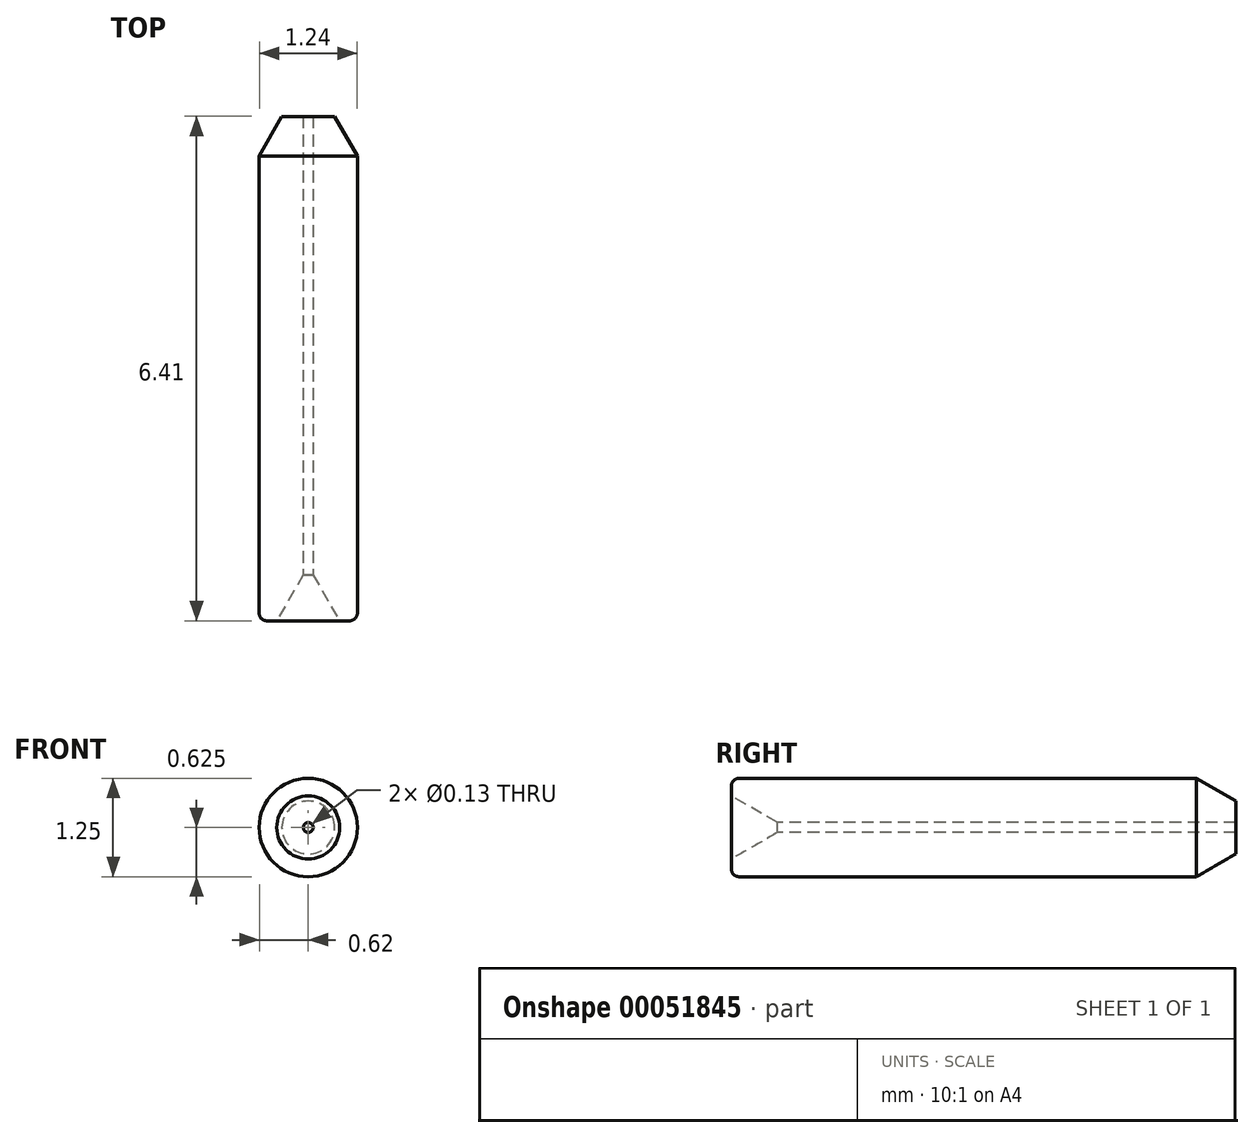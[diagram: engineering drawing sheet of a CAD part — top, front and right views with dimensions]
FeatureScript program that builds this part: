
annotation { "Feature Type Name" : "Feature", "Feature Type Description" : "" }
export const myFeature = defineFeature(function(context is Context, id is Id, definition is map)
    precondition{}
    {
        {
            var Q0;
            Q0=qCreatedBy(makeId("Right.planeOp"),FACE);
            var sketch = newSketch(context, id + "F0", { "sketchPlane" : qUnion([Q0])});
            skLineSegment(sketch, "E0.bottom", {"start": v(0.1, 0) * mm, "end": v(5.9, 0) * mm});
            skLineSegment(sketch, "E0.top", {"start": v(0.1, 1.25) * mm, "end": v(5.9, 1.25) * mm});
            skLineSegment(sketch, "E0.left", {"start": v(0, 0.1) * mm, "end": v(0, 0.22) * mm});
            skLineSegment(sketch, "E0.right", {"start": v(6.4, 0.29) * mm, "end": v(6.4, 0.56) * mm});
            skPoint(sketch, "E1.visualSharp", {"position": v(0, 1.25) * mm});
            skArc(sketch, "E1.filletArc", {"start": v(0.1, 1.25) * mm, "mid": v(0.03, 1.22) * mm, "end": v(0, 1.15) * mm});
            skPoint(sketch, "E2.visualSharp", {"position": v(0, 0) * mm});
            skArc(sketch, "E2.filletArc", {"start": v(0, 0.1) * mm, "mid": v(0.03, 0.03) * mm, "end": v(0.1, 0) * mm});
            skLineSegment(sketch, "E3", {"start": v(0, 0.62) * mm, "end": v(6.4, 0.62) * mm, "construction": true});
            skLineSegment(sketch, "E4", {"start": v(5.9, 1.25) * mm, "end": v(6.4, 0.96) * mm});
            skPoint(sketch, "E5.orphan", {"position": v(6.4, 1.25) * mm});
            skLineSegment(sketch, "E6", {"start": v(6.4, 0.29) * mm, "end": v(5.9, 0) * mm});
            skPoint(sketch, "E7.orphan", {"position": v(6.4, 0) * mm});
            skLineSegment(sketch, "E8", {"start": v(0, 1.15) * mm, "end": v(0, 1.02) * mm});
            skLineSegment(sketch, "E9", {"start": v(0, 1.02) * mm, "end": v(0.58, 0.69) * mm});
            skLineSegment(sketch, "E10", {"start": v(0.58, 0.56) * mm, "end": v(0, 0.22) * mm});
            skLineSegment(sketch, "E11.trimOffspring", {"start": v(0, 1.02) * mm, "end": v(0, 1.15) * mm});
            skLineSegment(sketch, "E12.bottom", {"start": v(0.58, 0.69) * mm, "end": v(6.4, 0.69) * mm});
            skLineSegment(sketch, "E12.top", {"start": v(0.58, 0.56) * mm, "end": v(6.4, 0.56) * mm});
            skLineSegment(sketch, "E13.trimOffspring", {"start": v(6.4, 0.69) * mm, "end": v(6.4, 0.96) * mm});
            skSolve(sketch);
        }
        {
            var Q0;
            Q0=makeQuery(id+"F0.imprint","IMPRINT",FACE,{"disambiguationData":[TD([[makeQuery(id+"F0.imprint","IMPRINT",EDGE,{"derivedFrom":sQuery(id+"F0.wireOp",EDGE,"E0.top")}),-1.0]])]});
            var Q1;
            Q1=makeQuery(id+"F0.imprint","IMPRINT",FACE,{"disambiguationData":[TD([[makeQuery(id+"F0.imprint","IMPRINT",EDGE,{"derivedFrom":sQuery(id+"F0.wireOp",EDGE,"E0.bottom")}),1.0]])]});
            var Q2;
            Q2=sQuery(id+"F0.wireOp",EDGE,"E3");
            revolve(context, id + "F1", {"entities" : qUnion([Q0, Q1]), "axis" : qUnion([Q2]), "revolveType" : RevolveType.FULL});
        }
    });
